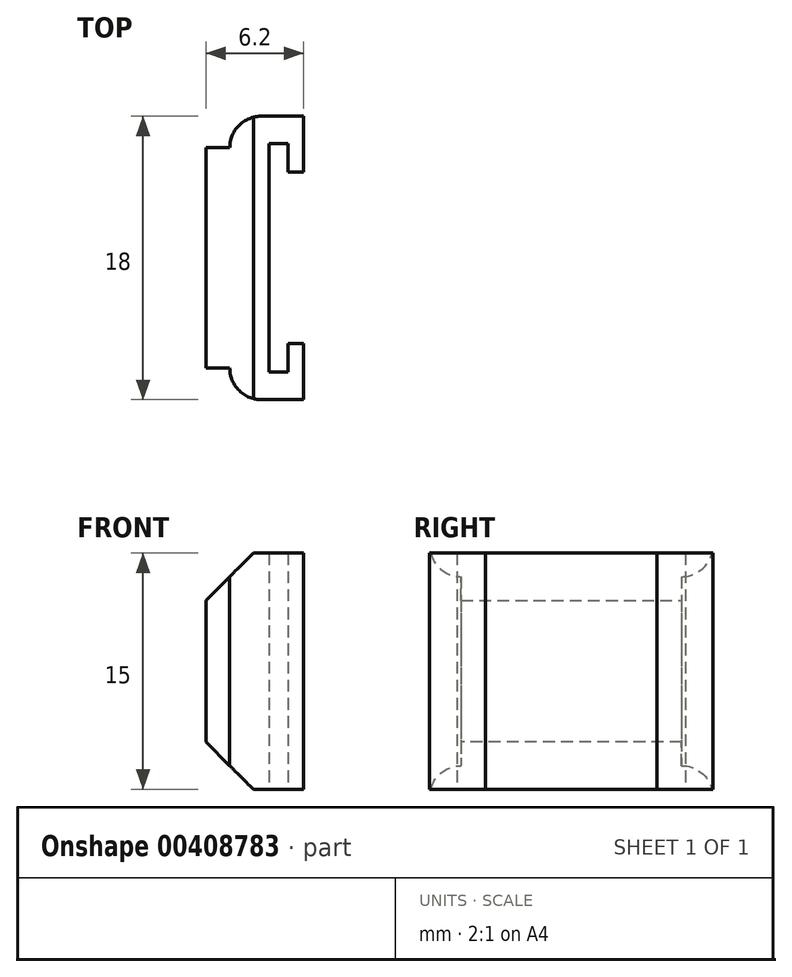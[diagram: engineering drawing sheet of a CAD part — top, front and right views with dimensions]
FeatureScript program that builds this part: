
annotation { "Feature Type Name" : "Feature", "Feature Type Description" : "" }
export const myFeature = defineFeature(function(context is Context, id is Id, definition is map)
    precondition{}
    {
        {
            var Q0;
            Q0=qCreatedBy(makeId("Top.planeOp"),FACE);
            var sketch = newSketch(context, id + "F0", { "sketchPlane" : qUnion([Q0])});
            skLineSegment(sketch, "E0", {"start": v(0, 2) * mm, "end": v(0, 16) * mm});
            skLineSegment(sketch, "E1", {"start": v(1.5, 18) * mm, "end": v(6.2, 18) * mm});
            skLineSegment(sketch, "E2", {"start": v(6.2, 18) * mm, "end": v(6.2, 14.45) * mm});
            skLineSegment(sketch, "E3", {"start": v(6.2, 14.45) * mm, "end": v(5.2, 14.45) * mm});
            skLineSegment(sketch, "E4", {"start": v(5.2, 14.45) * mm, "end": v(5.2, 16.25) * mm});
            skLineSegment(sketch, "E5", {"start": v(5.2, 16.25) * mm, "end": v(4, 16.25) * mm});
            skLineSegment(sketch, "E6", {"start": v(4, 16.25) * mm, "end": v(4, 1.75) * mm});
            skLineSegment(sketch, "E7", {"start": v(4, 1.75) * mm, "end": v(5.2, 1.75) * mm});
            skLineSegment(sketch, "E8", {"start": v(5.2, 1.75) * mm, "end": v(5.2, 3.55) * mm});
            skLineSegment(sketch, "E9", {"start": v(5.2, 3.55) * mm, "end": v(6.2, 3.55) * mm});
            skLineSegment(sketch, "E10", {"start": v(6.2, 3.55) * mm, "end": v(6.2, 0) * mm});
            skLineSegment(sketch, "E11", {"start": v(6.2, 0) * mm, "end": v(1.5, 0) * mm});
            skLineSegment(sketch, "E12", {"start": v(-12.04, 9) * mm, "end": v(24.92, 9) * mm, "construction": true});
            skPoint(sketch, "E12.endSnap0", {"position": v(13.77, 9) * mm});
            skLineSegment(sketch, "E13.top", {"start": v(0, 16) * mm, "end": v(1.5, 16) * mm});
            skLineSegment(sketch, "E13.right", {"start": v(1.5, 18) * mm, "end": v(1.5, 16) * mm});
            skLineSegment(sketch, "E14.top", {"start": v(0, 2) * mm, "end": v(1.5, 2) * mm});
            skLineSegment(sketch, "E14.right", {"start": v(1.5, 0) * mm, "end": v(1.5, 2) * mm});
            skSolve(sketch);
        }
        {
            var Q0;
            Q0=makeQuery(id+"F0.imprint","IMPRINT",FACE,{"disambiguationData":[TD([[makeQuery(id+"F0.imprint","IMPRINT",EDGE,{"derivedFrom":sQuery(id+"F0.wireOp",EDGE,"E0")}),-1.0]])]});
            extrude(context, id + "F1", {"entities" : qUnion([Q0]), "depth" : 15 * mm});
        }
        {
            var Q0;
            Q0=makeQuery(id+"F1.opExtrude","SWEPT_EDGE",EDGE,{"disambiguationData":[OSD([sQuery(id+"F0.wireOp",EDGE,"E11"),sQuery(id+"F0.wireOp",EDGE,"E14.right")])]});
            var Q1;
            Q1=makeQuery(id+"F1.opExtrude","SWEPT_EDGE",EDGE,{"disambiguationData":[OSD([sQuery(id+"F0.wireOp",EDGE,"E1"),sQuery(id+"F0.wireOp",EDGE,"E13.right")])]});
            fillet(context, id + "F2", {"entities" : qUnion([Q0, Q1]), "radius" : 2 * mm, "tangentPropagation" : true, "allowEdgeOverflow" : false});
        }
        {
            var Q0;
            Q0=makeQuery(id+"F1.opExtrude","CAP_EDGE",EDGE,{"disambiguationData":[OSD([sQuery(id+"F0.wireOp",EDGE,"E0")])],"isStart":true});
            var Q1;
            Q1=makeQuery(id+"F1.opExtrude","CAP_EDGE",EDGE,{"disambiguationData":[OSD([sQuery(id+"F0.wireOp",EDGE,"E0")])],"isStart":false});
            chamfer(context, id + "F3", {"entities" : qUnion([Q0, Q1]), "width" : 3 * mm, "tangentPropagation" : true});
        }
    });
